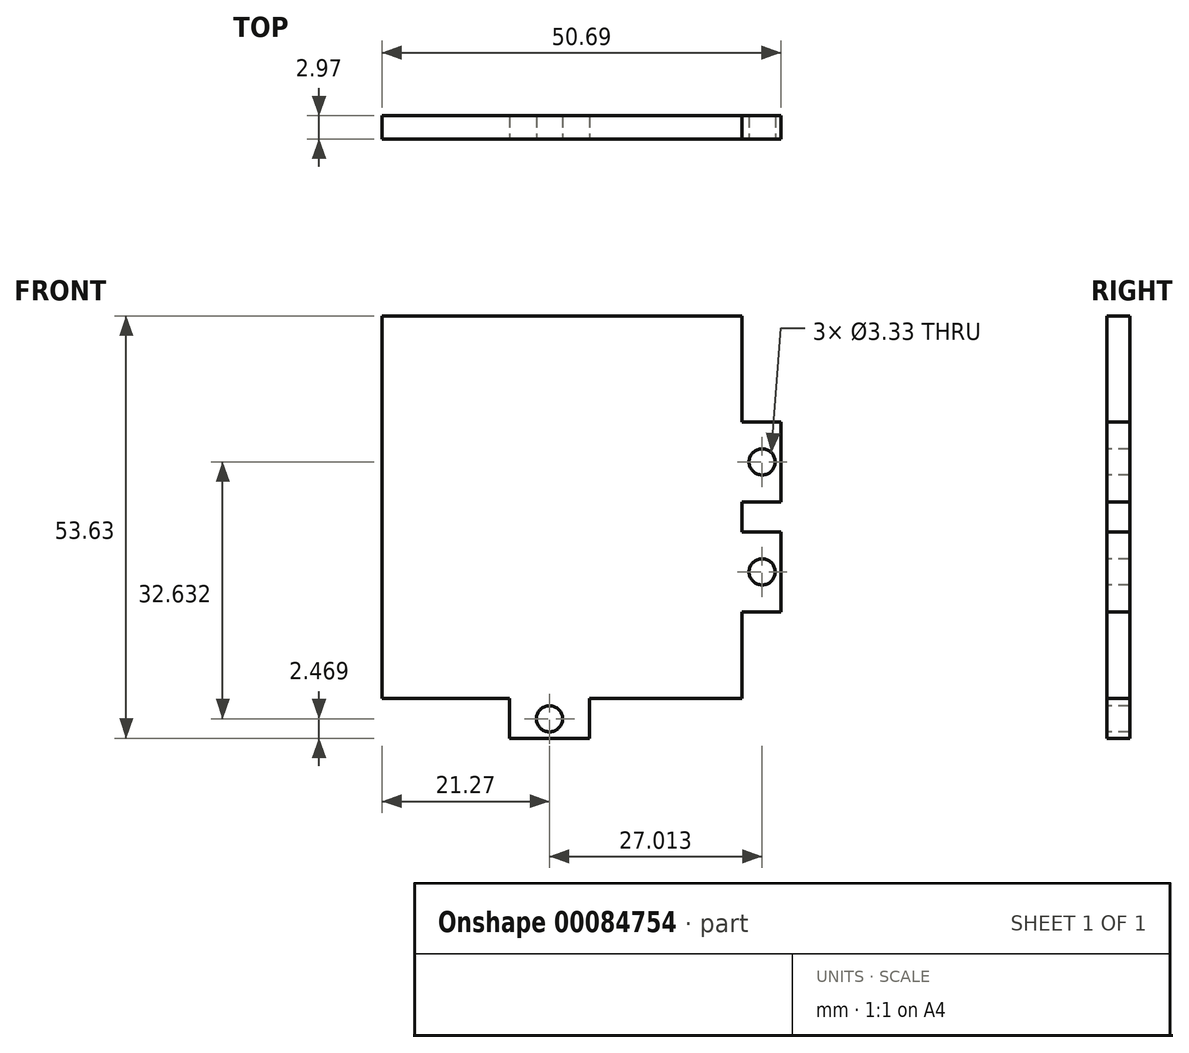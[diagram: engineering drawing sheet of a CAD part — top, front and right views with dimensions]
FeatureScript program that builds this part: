
annotation { "Feature Type Name" : "Feature", "Feature Type Description" : "" }
export const myFeature = defineFeature(function(context is Context, id is Id, definition is map)
    precondition{}
    {
        {
            var Q0;
            Q0=qCreatedBy(makeId("Front.planeOp"),FACE);
            var sketch = newSketch(context, id + "F0", { "sketchPlane" : qUnion([Q0])});
            skLineSegment(sketch, "E0.bottom", {"start": v(25.4, 25.4) * mm, "end": v(-25.4, 25.4) * mm});
            skLineSegment(sketch, "E0.top", {"start": v(25.4, -25.4) * mm, "end": v(-25.4, -25.4) * mm});
            skLineSegment(sketch, "E0.left", {"start": v(25.4, 25.4) * mm, "end": v(25.4, -25.4) * mm});
            skLineSegment(sketch, "E0.right", {"start": v(-25.4, 25.4) * mm, "end": v(-25.4, -25.4) * mm});
            skPoint(sketch, "E0.middle", {"position": v(0, 0) * mm});
            skSolve(sketch);
        }
        {
            var Q0;
            Q0=makeQuery(id+"F0.imprint","IMPRINT",FACE,{"disambiguationData":[TD([[makeQuery(id+"F0.imprint","IMPRINT",EDGE,{"derivedFrom":sQuery(id+"F0.wireOp",EDGE,"E0.bottom")}),1.0]])]});
            extrude(context, id + "F1", {"entities" : qUnion([Q0]), "depth" : 2.97 * mm});
        }
        {
            var Q0;
            Q0=makeQuery(id+"F1.opExtrude","CAP_FACE",FACE,{"disambiguationData":[OSD([sQuery(id+"F0.wireOp",EDGE,"E0.bottom"),sQuery(id+"F0.wireOp",EDGE,"E0.top"),sQuery(id+"F0.wireOp",EDGE,"E0.left"),sQuery(id+"F0.wireOp",EDGE,"E0.right")])],"isStart":false});
            var sketch = newSketch(context, id + "F2", { "sketchPlane" : qUnion([Q0])});
            skLineSegment(sketch, "E1.bottom", {"start": v(20.2, 11.95) * mm, "end": v(25.29, 11.95) * mm});
            skLineSegment(sketch, "E1.top", {"start": v(20.2, 1.8) * mm, "end": v(25.29, 1.8) * mm});
            skLineSegment(sketch, "E1.left", {"start": v(20.2, 11.95) * mm, "end": v(20.2, 1.8) * mm});
            skLineSegment(sketch, "E1.right", {"start": v(25.29, 11.95) * mm, "end": v(25.29, 1.8) * mm});
            skLineSegment(sketch, "E2.bottom", {"start": v(20.2, -2.02) * mm, "end": v(25.29, -2.02) * mm});
            skLineSegment(sketch, "E2.top", {"start": v(20.2, -12.18) * mm, "end": v(25.29, -12.18) * mm});
            skLineSegment(sketch, "E2.left", {"start": v(20.2, -2.02) * mm, "end": v(20.2, -12.18) * mm});
            skLineSegment(sketch, "E2.right", {"start": v(25.29, -2.02) * mm, "end": v(25.29, -12.18) * mm});
            skSolve(sketch);
        }
        {
            var Q0;
            Q0=makeQuery(id+"F1.opExtrude","CAP_FACE",FACE,{"disambiguationData":[OSD([sQuery(id+"F0.wireOp",EDGE,"E0.bottom"),sQuery(id+"F0.wireOp",EDGE,"E0.top"),sQuery(id+"F0.wireOp",EDGE,"E0.left"),sQuery(id+"F0.wireOp",EDGE,"E0.right")])],"isStart":false});
            var sketch = newSketch(context, id + "F3", { "sketchPlane" : qUnion([Q0])});
            skLineSegment(sketch, "E3.bottom", {"start": v(25.4, 25.4) * mm, "end": v(20.32, 25.4) * mm});
            skLineSegment(sketch, "E3.top", {"start": v(25.4, -25.4) * mm, "end": v(20.32, -25.4) * mm});
            skLineSegment(sketch, "E3.left", {"start": v(25.4, 25.4) * mm, "end": v(25.4, -25.4) * mm});
            skLineSegment(sketch, "E3.right", {"start": v(20.32, 25.4) * mm, "end": v(20.32, -25.4) * mm});
            skSolve(sketch);
        }
        {
            var Q0;
            Q0 = qSketchRegion(id + "F3", true);
            extrude(context, id + "F4", {"entities" : qUnion([Q0]), "operationType" : NewBodyOperationType.REMOVE, "endBound" : BoundingType.THROUGH_ALL, "oppositeDirection" : true, "depth" : 25.4 * mm});
        }
        {
            var Q0;
            Q0 = qSketchRegion(id + "F2", true);
            extrude(context, id + "F5", {"entities" : qUnion([Q0]), "operationType" : NewBodyOperationType.ADD, "oppositeDirection" : true, "depth" : 2.97 * mm});
        }
        {
            var Q0;
            Q0=makeQuery(id+"F5.boolean.opBoolean","MERGE",FACE,{"derivedFrom":[makeQuery(id+"F1.opExtrude","CAP_FACE",FACE,{"disambiguationData":[OSD([sQuery(id+"F0.wireOp",EDGE,"E0.bottom"),sQuery(id+"F0.wireOp",EDGE,"E0.top"),sQuery(id+"F0.wireOp",EDGE,"E0.left"),sQuery(id+"F0.wireOp",EDGE,"E0.right")])],"isStart":false}),makeQuery(id+"F5.opExtrude","CAP_FACE",FACE,{"disambiguationData":[OSD([sQuery(id+"F2.wireOp",EDGE,"E1.bottom"),sQuery(id+"F2.wireOp",EDGE,"E1.top"),sQuery(id+"F2.wireOp",EDGE,"E1.left"),sQuery(id+"F2.wireOp",EDGE,"E1.right")])],"isStart":true}),makeQuery(id+"F5.opExtrude","CAP_FACE",FACE,{"disambiguationData":[OSD([sQuery(id+"F2.wireOp",EDGE,"E2.bottom"),sQuery(id+"F2.wireOp",EDGE,"E2.top"),sQuery(id+"F2.wireOp",EDGE,"E2.left"),sQuery(id+"F2.wireOp",EDGE,"E2.right")])],"isStart":true})]});
            var sketch = newSketch(context, id + "F6", { "sketchPlane" : qUnion([Q0])});
            skLineSegment(sketch, "E4.bottom", {"start": v(20.32, -23.15) * mm, "end": v(-25.4, -23.15) * mm});
            skLineSegment(sketch, "E4.top", {"start": v(20.32, -25.4) * mm, "end": v(-25.4, -25.4) * mm});
            skLineSegment(sketch, "E4.left", {"start": v(20.32, -23.15) * mm, "end": v(20.32, -25.4) * mm});
            skLineSegment(sketch, "E4.right", {"start": v(-25.4, -23.15) * mm, "end": v(-25.4, -25.4) * mm});
            skSolve(sketch);
        }
        {
            var Q0;
            Q0 = qSketchRegion(id + "F6", true);
            extrude(context, id + "F7", {"entities" : qUnion([Q0]), "operationType" : NewBodyOperationType.REMOVE, "endBound" : BoundingType.THROUGH_ALL, "oppositeDirection" : true, "depth" : 25.4 * mm});
        }
        {
            var Q0;
            Q0=makeQuery(id+"F5.boolean.opBoolean","MERGE",FACE,{"derivedFrom":[makeQuery(id+"F1.opExtrude","CAP_FACE",FACE,{"disambiguationData":[OSD([sQuery(id+"F0.wireOp",EDGE,"E0.bottom"),sQuery(id+"F0.wireOp",EDGE,"E0.top"),sQuery(id+"F0.wireOp",EDGE,"E0.left"),sQuery(id+"F0.wireOp",EDGE,"E0.right")])],"isStart":false}),makeQuery(id+"F5.opExtrude","CAP_FACE",FACE,{"disambiguationData":[OSD([sQuery(id+"F2.wireOp",EDGE,"E1.bottom"),sQuery(id+"F2.wireOp",EDGE,"E1.top"),sQuery(id+"F2.wireOp",EDGE,"E1.left"),sQuery(id+"F2.wireOp",EDGE,"E1.right")])],"isStart":true}),makeQuery(id+"F5.opExtrude","CAP_FACE",FACE,{"disambiguationData":[OSD([sQuery(id+"F2.wireOp",EDGE,"E2.bottom"),sQuery(id+"F2.wireOp",EDGE,"E2.top"),sQuery(id+"F2.wireOp",EDGE,"E2.left"),sQuery(id+"F2.wireOp",EDGE,"E2.right")])],"isStart":true})]});
            var sketch = newSketch(context, id + "F8", { "sketchPlane" : qUnion([Q0])});
            skCircle(sketch, "E5", {"center": v(22.88, 6.87) * mm, "radius": 1.66 * mm});
            skPoint(sketch, "E5.centerSnap0", {"position": v(25.29, 6.87) * mm});
            skCircle(sketch, "E6", {"center": v(22.88, -7.1) * mm, "radius": 1.66 * mm});
            skPoint(sketch, "E6.centerSnap0", {"position": v(25.29, -7.1) * mm});
            skSolve(sketch);
        }
        {
            var Q0;
            Q0 = qSketchRegion(id + "F8", true);
            extrude(context, id + "F9", {"entities" : qUnion([Q0]), "operationType" : NewBodyOperationType.REMOVE, "endBound" : BoundingType.THROUGH_ALL, "oppositeDirection" : true, "depth" : 25.4 * mm});
        }
        {
            var Q0;
            Q0=makeQuery(id+"F5.boolean.opBoolean","MERGE",FACE,{"derivedFrom":[makeQuery(id+"F1.opExtrude","CAP_FACE",FACE,{"disambiguationData":[OSD([sQuery(id+"F0.wireOp",EDGE,"E0.bottom"),sQuery(id+"F0.wireOp",EDGE,"E0.top"),sQuery(id+"F0.wireOp",EDGE,"E0.left"),sQuery(id+"F0.wireOp",EDGE,"E0.right")])],"isStart":false}),makeQuery(id+"F5.opExtrude","CAP_FACE",FACE,{"disambiguationData":[OSD([sQuery(id+"F2.wireOp",EDGE,"E1.bottom"),sQuery(id+"F2.wireOp",EDGE,"E1.top"),sQuery(id+"F2.wireOp",EDGE,"E1.left"),sQuery(id+"F2.wireOp",EDGE,"E1.right")])],"isStart":true}),makeQuery(id+"F5.opExtrude","CAP_FACE",FACE,{"disambiguationData":[OSD([sQuery(id+"F2.wireOp",EDGE,"E2.bottom"),sQuery(id+"F2.wireOp",EDGE,"E2.top"),sQuery(id+"F2.wireOp",EDGE,"E2.left"),sQuery(id+"F2.wireOp",EDGE,"E2.right")])],"isStart":true})]});
            var sketch = newSketch(context, id + "F10", { "sketchPlane" : qUnion([Q0])});
            skLineSegment(sketch, "E7", {"start": v(-25.4, -23.15) * mm, "end": v(-9.21, -23.15) * mm});
            skLineSegment(sketch, "E8.bottom", {"start": v(-9.21, -23.15) * mm, "end": v(0.95, -23.15) * mm});
            skLineSegment(sketch, "E8.top", {"start": v(-9.21, -28.23) * mm, "end": v(0.95, -28.23) * mm});
            skLineSegment(sketch, "E8.left", {"start": v(-9.21, -23.15) * mm, "end": v(-9.21, -28.23) * mm});
            skLineSegment(sketch, "E8.right", {"start": v(0.95, -23.15) * mm, "end": v(0.95, -28.23) * mm});
            skCircle(sketch, "E9", {"center": v(-4.13, -25.76) * mm, "radius": 1.66 * mm});
            skPoint(sketch, "E9.centerSnap0", {"position": v(-4.13, -23.15) * mm});
            skSolve(sketch);
        }
        {
            var Q0;
            Q0 = qSketchRegion(id + "F10", true);
            extrude(context, id + "F11", {"entities" : qUnion([Q0]), "operationType" : NewBodyOperationType.ADD, "oppositeDirection" : true, "depth" : 2.97 * mm});
        }
    });
